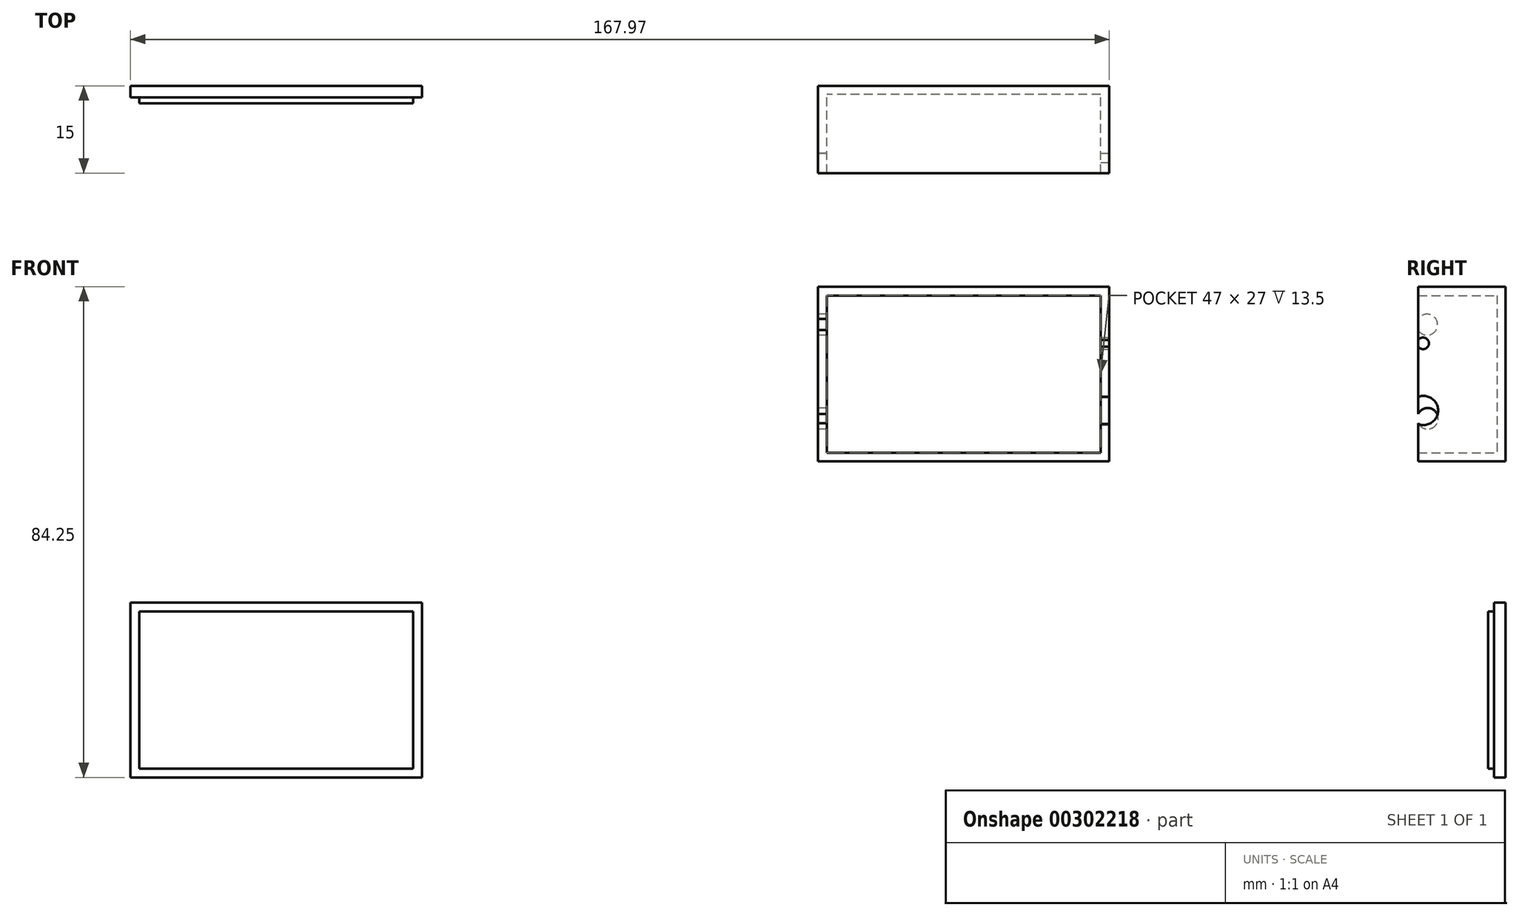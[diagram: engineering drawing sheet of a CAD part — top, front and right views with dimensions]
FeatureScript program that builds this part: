
annotation { "Feature Type Name" : "Feature", "Feature Type Description" : "" }
export const myFeature = defineFeature(function(context is Context, id is Id, definition is map)
    precondition{}
    {
        {
            var Q0;
            Q0=qCreatedBy(makeId("Front.planeOp"),FACE);
            var sketch = newSketch(context, id + "F0", { "sketchPlane" : qUnion([Q0])});
            skLineSegment(sketch, "E0.bottom", {"start": v(-55.27, 21.25) * mm, "end": v(-105.27, 21.25) * mm});
            skLineSegment(sketch, "E0.top", {"start": v(-55.27, -8.75) * mm, "end": v(-105.27, -8.75) * mm});
            skLineSegment(sketch, "E0.left", {"start": v(-55.27, 21.25) * mm, "end": v(-55.27, -8.75) * mm});
            skLineSegment(sketch, "E0.right", {"start": v(-105.27, 21.25) * mm, "end": v(-105.27, -8.75) * mm});
            skLineSegment(sketch, "E1.bottom", {"start": v(-173.24, -33) * mm, "end": v(-223.24, -33) * mm});
            skLineSegment(sketch, "E1.top", {"start": v(-173.24, -63) * mm, "end": v(-223.24, -63) * mm});
            skLineSegment(sketch, "E1.left", {"start": v(-173.24, -33) * mm, "end": v(-173.24, -63) * mm});
            skLineSegment(sketch, "E1.right", {"start": v(-223.24, -33) * mm, "end": v(-223.24, -63) * mm});
            skSolve(sketch);
        }
        {
            var Q0;
            Q0=makeQuery(id+"F0.imprint","IMPRINT",FACE,{"disambiguationData":[TD([[makeQuery(id+"F0.imprint","IMPRINT",EDGE,{"derivedFrom":sQuery(id+"F0.wireOp",EDGE,"E0.bottom")}),1.0]])]});
            extrude(context, id + "F1", {"entities" : qUnion([Q0]), "depth" : 15 * mm});
        }
        {
            var Q0;
            Q0=makeQuery(id+"F1.opExtrude","CAP_FACE",FACE,{"disambiguationData":[OSD([sQuery(id+"F0.wireOp",EDGE,"E0.bottom"),sQuery(id+"F0.wireOp",EDGE,"E0.top"),sQuery(id+"F0.wireOp",EDGE,"E0.left"),sQuery(id+"F0.wireOp",EDGE,"E0.right")])],"isStart":false});
            shell(context, id + "F2", {"entities" : qUnion([Q0]), "thickness" : 1.5 * mm});
        }
        {
            var Q0;
            Q0=makeQuery(id+"F0.imprint","IMPRINT",FACE,{"disambiguationData":[TD([[makeQuery(id+"F0.imprint","IMPRINT",EDGE,{"derivedFrom":sQuery(id+"F0.wireOp",EDGE,"E1.bottom")}),1.0]])]});
            extrude(context, id + "F3", {"entities" : qUnion([Q0]), "depth" : 2 * mm});
        }
        {
            var Q0;
            Q0=makeQuery(id+"F3.opExtrude","CAP_FACE",FACE,{"disambiguationData":[OSD([sQuery(id+"F0.wireOp",EDGE,"E1.bottom"),sQuery(id+"F0.wireOp",EDGE,"E1.top"),sQuery(id+"F0.wireOp",EDGE,"E1.left"),sQuery(id+"F0.wireOp",EDGE,"E1.right")])],"isStart":false});
            shell(context, id + "F4", {"entities" : qUnion([Q0]), "thickness" : 1.5 * mm});
        }
        {
            var Q0;
            Q0=makeQuery(id+"F4.opShell","OFFSET_FACE",FACE,{"disambiguationData":[OSD([sQuery(id+"F0.wireOp",EDGE,"E1.bottom"),sQuery(id+"F0.wireOp",EDGE,"E1.top"),sQuery(id+"F0.wireOp",EDGE,"E1.left"),sQuery(id+"F0.wireOp",EDGE,"E1.right")])]});
            extrude(context, id + "F5", {"entities" : qUnion([Q0]), "operationType" : NewBodyOperationType.ADD, "depth" : 1.5 * mm});
        }
        {
            var Q0;
            Q0=makeQuery(id+"F1.opExtrude","SWEPT_FACE",FACE,{"disambiguationData":[OSD([sQuery(id+"F0.wireOp",EDGE,"E0.right")])]});
            var sketch = newSketch(context, id + "F6", { "sketchPlane" : qUnion([Q0])});
            skArc(sketch, "E2", {"start": v(15, 15.69) * mm, "mid": v(11.67, 14.73) * mm, "end": v(15, 13.78) * mm});
            skArc(sketch, "E3", {"start": v(15, -0.6) * mm, "mid": v(11.58, -1.38) * mm, "end": v(15, -2.17) * mm});
            skSolve(sketch);
        }
        {
            var Q0;
            {var subQ0=sQuery(id+"F6.wireOp",EDGE,"E3");Q0=makeQuery(id+"F6.imprint","IMPRINT",FACE,{"disambiguationData":[TD([[makeQuery(id+"F6.imprint","IMPRINT",EDGE,{"derivedFrom":subQ0}),1.0]])]});}
            var Q1;
            {var subQ0=sQuery(id+"F6.wireOp",EDGE,"E2");Q1=makeQuery(id+"F6.imprint","IMPRINT",FACE,{"disambiguationData":[TD([[makeQuery(id+"F6.imprint","IMPRINT",EDGE,{"derivedFrom":subQ0}),1.0]])]});}
            extrude(context, id + "F7", {"entities" : qUnion([Q0, Q1]), "operationType" : NewBodyOperationType.REMOVE, "oppositeDirection" : true, "depth" : 5 * mm});
        }
        {
            var Q0;
            Q0=makeQuery(id+"F1.opExtrude","SWEPT_FACE",FACE,{"disambiguationData":[OSD([sQuery(id+"F0.wireOp",EDGE,"E0.left")])]});
            var sketch = newSketch(context, id + "F8", { "sketchPlane" : qUnion([Q0])});
            skArc(sketch, "E4", {"start": v(-15, -2.33) * mm, "mid": v(-11.59, 0) * mm, "end": v(-15, 2.33) * mm});
            skArc(sketch, "E5", {"start": v(-15, 10.98) * mm, "mid": v(-13.16, 11.52) * mm, "end": v(-15, 12.07) * mm});
            skSolve(sketch);
        }
        {
            var Q0;
            Q0 = qSketchRegion(id + "F8", true);
            var Q1;
            {var subQ0=sQuery(id+"F8.wireOp",EDGE,"E4");Q1=makeQuery(id+"F8.imprint","IMPRINT",FACE,{"disambiguationData":[TD([[makeQuery(id+"F8.imprint","IMPRINT",EDGE,{"derivedFrom":subQ0}),1.0]])]});}
            var Q2;
            {var subQ0=sQuery(id+"F8.wireOp",EDGE,"E5");Q2=makeQuery(id+"F8.imprint","IMPRINT",FACE,{"disambiguationData":[TD([[makeQuery(id+"F8.imprint","IMPRINT",EDGE,{"derivedFrom":subQ0}),1.0]])]});}
            extrude(context, id + "F9", {"entities" : qUnion([Q0, Q1, Q2]), "operationType" : NewBodyOperationType.REMOVE, "oppositeDirection" : true, "depth" : 5 * mm});
        }
    });
